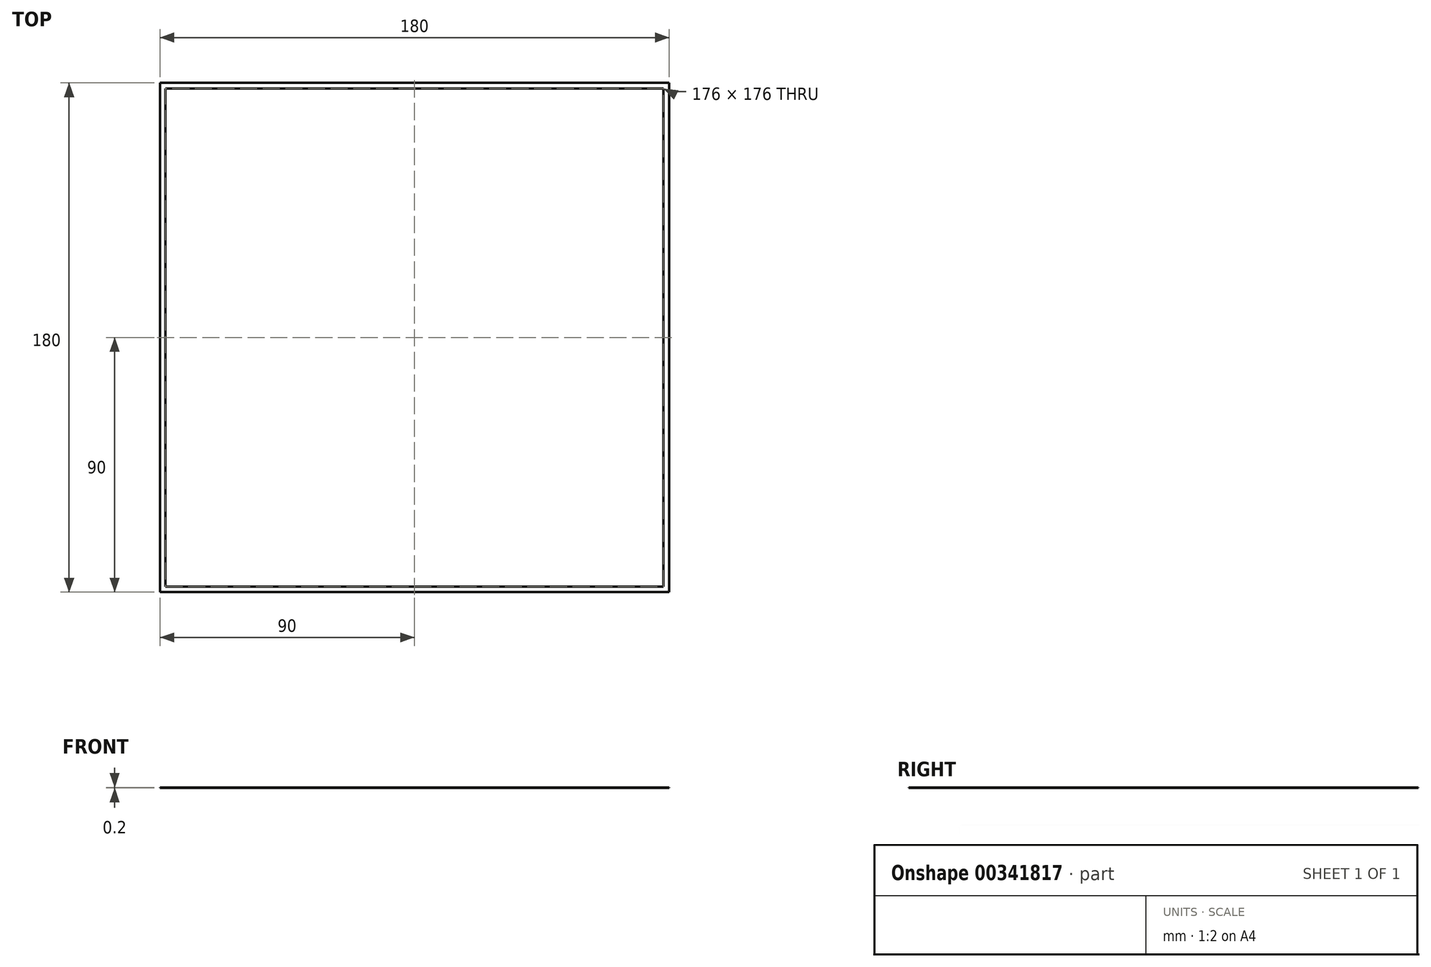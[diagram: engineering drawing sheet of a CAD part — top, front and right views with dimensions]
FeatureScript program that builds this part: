
annotation { "Feature Type Name" : "Feature", "Feature Type Description" : "" }
export const myFeature = defineFeature(function(context is Context, id is Id, definition is map)
    precondition{}
    {
        {
            var Q0;
            Q0=qCreatedBy(makeId("Top.planeOp"),FACE);
            var sketch = newSketch(context, id + "F0", { "sketchPlane" : qUnion([Q0])});
            skLineSegment(sketch, "E0.bottom", {"start": v(88, 88) * mm, "end": v(-88, 88) * mm});
            skLineSegment(sketch, "E0.top", {"start": v(88, -88) * mm, "end": v(-88, -88) * mm});
            skLineSegment(sketch, "E0.left", {"start": v(88, 88) * mm, "end": v(88, -88) * mm});
            skLineSegment(sketch, "E0.right", {"start": v(-88, 88) * mm, "end": v(-88, -88) * mm});
            skPoint(sketch, "E0.middle", {"position": v(0, 0) * mm});
            skLineSegment(sketch, "E1.bottom", {"start": v(90, 90) * mm, "end": v(-90, 90) * mm});
            skLineSegment(sketch, "E1.top", {"start": v(90, -90) * mm, "end": v(-90, -90) * mm});
            skLineSegment(sketch, "E1.left", {"start": v(90, 90) * mm, "end": v(90, -90) * mm});
            skLineSegment(sketch, "E1.right", {"start": v(-90, 90) * mm, "end": v(-90, -90) * mm});
            skSolve(sketch);
        }
        {
            var Q0;
            Q0=makeQuery(id+"F0.imprint","IMPRINT",FACE,{"disambiguationData":[TD([[makeQuery(id+"F0.imprint","IMPRINT",EDGE,{"derivedFrom":sQuery(id+"F0.wireOp",EDGE,"E0.bottom")}),-1.0]])]});
            extrude(context, id + "F1", {"entities" : qUnion([Q0]), "depth" : 0.2 * mm});
        }
    });
